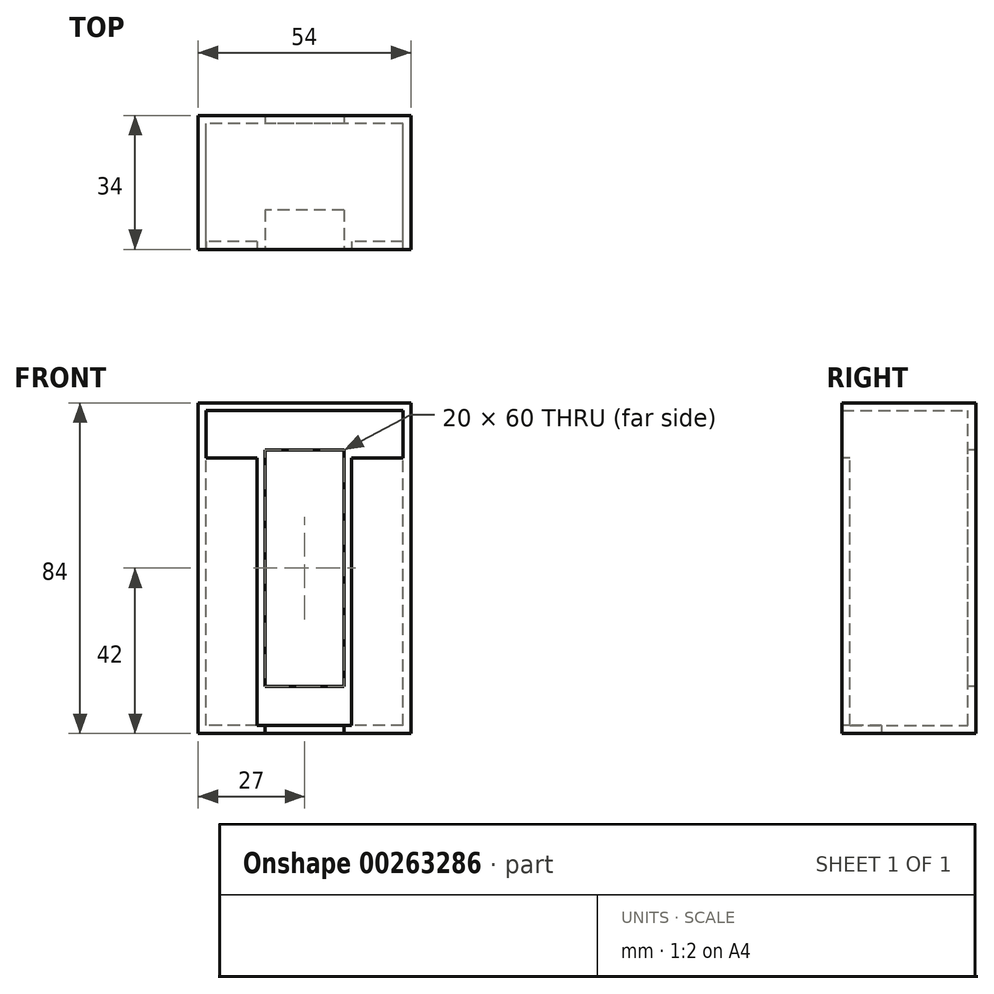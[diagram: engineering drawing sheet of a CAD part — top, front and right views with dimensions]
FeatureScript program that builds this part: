
annotation { "Feature Type Name" : "Feature", "Feature Type Description" : "" }
export const myFeature = defineFeature(function(context is Context, id is Id, definition is map)
    precondition{}
    {
        {
            var Q0;
            Q0=qCreatedBy(makeId("Front.planeOp"),FACE);
            var sketch = newSketch(context, id + "F0", { "sketchPlane" : qUnion([Q0])});
            skLineSegment(sketch, "E0.bottom", {"start": v(27, -42) * mm, "end": v(-27, -42) * mm});
            skLineSegment(sketch, "E0.top", {"start": v(27, 42) * mm, "end": v(-27, 42) * mm});
            skLineSegment(sketch, "E0.left", {"start": v(27, -42) * mm, "end": v(27, 42) * mm});
            skLineSegment(sketch, "E0.right", {"start": v(-27, -42) * mm, "end": v(-27, 42) * mm});
            skPoint(sketch, "E0.middle", {"position": v(0, 0) * mm});
            skSolve(sketch);
        }
        {
            var Q0;
            Q0 = qSketchRegion(id + "F0", true);
            extrude(context, id + "F1", {"entities" : qUnion([Q0]), "depth" : 34 * mm});
        }
        {
            var Q0;
            Q0=makeQuery(id+"F1.opExtrude","CAP_FACE",FACE,{"disambiguationData":[OSD([sQuery(id+"F0.wireOp",EDGE,"E0.bottom"),sQuery(id+"F0.wireOp",EDGE,"E0.top"),sQuery(id+"F0.wireOp",EDGE,"E0.left"),sQuery(id+"F0.wireOp",EDGE,"E0.right")])],"isStart":false});
            shell(context, id + "F2", {"entities" : qUnion([Q0]), "thickness" : 2 * mm});
        }
        {
            var Q0;
            Q0=makeQuery(id+"F2.opShell","OFFSET_FACE",FACE,{"disambiguationData":[OSD([sQuery(id+"F0.wireOp",EDGE,"E0.bottom"),sQuery(id+"F0.wireOp",EDGE,"E0.top"),sQuery(id+"F0.wireOp",EDGE,"E0.left"),sQuery(id+"F0.wireOp",EDGE,"E0.right")])]});
            var sketch = newSketch(context, id + "F3", { "sketchPlane" : qUnion([Q0])});
            skLineSegment(sketch, "E1.bottom", {"start": v(10, -30) * mm, "end": v(-10, -30) * mm});
            skLineSegment(sketch, "E1.top", {"start": v(10, 30) * mm, "end": v(-10, 30) * mm});
            skLineSegment(sketch, "E1.left", {"start": v(10, -30) * mm, "end": v(10, 30) * mm});
            skLineSegment(sketch, "E1.right", {"start": v(-10, -30) * mm, "end": v(-10, 30) * mm});
            skPoint(sketch, "E1.middle", {"position": v(0, 0) * mm});
            skSolve(sketch);
        }
        {
            var Q0;
            Q0 = qSketchRegion(id + "F3", true);
            extrude(context, id + "F4", {"entities" : qUnion([Q0]), "operationType" : NewBodyOperationType.REMOVE, "oppositeDirection" : true, "depth" : 25 * mm});
        }
        {
            var Q0;
            Q0=makeQuery(id+"F1.opExtrude","CAP_FACE",FACE,{"disambiguationData":[OSD([sQuery(id+"F0.wireOp",EDGE,"E0.bottom"),sQuery(id+"F0.wireOp",EDGE,"E0.top"),sQuery(id+"F0.wireOp",EDGE,"E0.left"),sQuery(id+"F0.wireOp",EDGE,"E0.right")])],"isStart":false});
            var sketch = newSketch(context, id + "F5", { "sketchPlane" : qUnion([Q0])});
            skLineSegment(sketch, "E2.bottom", {"start": v(-27, -42) * mm, "end": v(-12, -42) * mm});
            skLineSegment(sketch, "E2.top", {"start": v(-27, 28) * mm, "end": v(-12, 28) * mm});
            skLineSegment(sketch, "E2.left", {"start": v(-27, -42) * mm, "end": v(-27, 28) * mm});
            skLineSegment(sketch, "E2.right", {"start": v(-12, -42) * mm, "end": v(-12, 28) * mm});
            skSolve(sketch);
        }
        {
            var Q0;
            Q0 = qSketchRegion(id + "F5", true);
            extrude(context, id + "F6", {"entities" : qUnion([Q0]), "operationType" : NewBodyOperationType.ADD, "oppositeDirection" : true, "depth" : 2 * mm});
        }
        {
            var Q0;
            Q0=makeQuery(id+"F6.boolean.opBoolean","MERGE",FACE,{"derivedFrom":[makeQuery(id+"F1.opExtrude","CAP_FACE",FACE,{"disambiguationData":[OSD([sQuery(id+"F0.wireOp",EDGE,"E0.bottom"),sQuery(id+"F0.wireOp",EDGE,"E0.top"),sQuery(id+"F0.wireOp",EDGE,"E0.left"),sQuery(id+"F0.wireOp",EDGE,"E0.right")])],"isStart":false}),makeQuery(id+"F6.opExtrude","CAP_FACE",FACE,{"disambiguationData":[OSD([sQuery(id+"F5.wireOp",EDGE,"E2.bottom"),sQuery(id+"F5.wireOp",EDGE,"E2.top"),sQuery(id+"F5.wireOp",EDGE,"E2.left"),sQuery(id+"F5.wireOp",EDGE,"E2.right")])],"isStart":true})]});
            var sketch = newSketch(context, id + "F7", { "sketchPlane" : qUnion([Q0])});
            skLineSegment(sketch, "E3.bottom", {"start": v(27, -42) * mm, "end": v(12, -42) * mm});
            skLineSegment(sketch, "E3.top", {"start": v(27, 28) * mm, "end": v(12, 28) * mm});
            skLineSegment(sketch, "E3.left", {"start": v(27, -42) * mm, "end": v(27, 28) * mm});
            skLineSegment(sketch, "E3.right", {"start": v(12, -42) * mm, "end": v(12, 28) * mm});
            skSolve(sketch);
        }
        {
            var Q0;
            Q0 = qSketchRegion(id + "F7", true);
            extrude(context, id + "F8", {"entities" : qUnion([Q0]), "operationType" : NewBodyOperationType.ADD, "oppositeDirection" : true, "depth" : 2 * mm});
        }
        {
            var Q0;
            Q0=makeQuery(id+"F8.boolean.opBoolean","MERGE",FACE,{"derivedFrom":[makeQuery(id+"F6.boolean.opBoolean","MERGE",FACE,{"derivedFrom":[makeQuery(id+"F1.opExtrude","CAP_FACE",FACE,{"disambiguationData":[OSD([sQuery(id+"F0.wireOp",EDGE,"E0.bottom"),sQuery(id+"F0.wireOp",EDGE,"E0.top"),sQuery(id+"F0.wireOp",EDGE,"E0.left"),sQuery(id+"F0.wireOp",EDGE,"E0.right")])],"isStart":false}),makeQuery(id+"F6.opExtrude","CAP_FACE",FACE,{"disambiguationData":[OSD([sQuery(id+"F5.wireOp",EDGE,"E2.bottom"),sQuery(id+"F5.wireOp",EDGE,"E2.top"),sQuery(id+"F5.wireOp",EDGE,"E2.left"),sQuery(id+"F5.wireOp",EDGE,"E2.right")])],"isStart":true})]}),makeQuery(id+"F8.opExtrude","CAP_FACE",FACE,{"disambiguationData":[OSD([sQuery(id+"F7.wireOp",EDGE,"E3.bottom"),sQuery(id+"F7.wireOp",EDGE,"E3.top"),sQuery(id+"F7.wireOp",EDGE,"E3.left"),sQuery(id+"F7.wireOp",EDGE,"E3.right")])],"isStart":true})]});
            var sketch = newSketch(context, id + "F9", { "sketchPlane" : qUnion([Q0])});
            skLineSegment(sketch, "E4.bottom", {"start": v(0, -40) * mm, "end": v(-10, -40) * mm});
            skLineSegment(sketch, "E4.top", {"start": v(0, -42) * mm, "end": v(-10, -42) * mm});
            skLineSegment(sketch, "E4.left", {"start": v(0, -40) * mm, "end": v(0, -42) * mm});
            skLineSegment(sketch, "E4.right", {"start": v(-10, -40) * mm, "end": v(-10, -42) * mm});
            skLineSegment(sketch, "E5.bottom", {"start": v(0, -40) * mm, "end": v(10, -40) * mm});
            skLineSegment(sketch, "E5.top", {"start": v(0, -42) * mm, "end": v(10, -42) * mm});
            skLineSegment(sketch, "E5.right", {"start": v(10, -40) * mm, "end": v(10, -42) * mm});
            skSolve(sketch);
        }
        {
            var Q0;
            Q0 = qSketchRegion(id + "F9", true);
            extrude(context, id + "F10", {"entities" : qUnion([Q0]), "operationType" : NewBodyOperationType.REMOVE, "oppositeDirection" : true, "depth" : 10 * mm});
        }
    });
